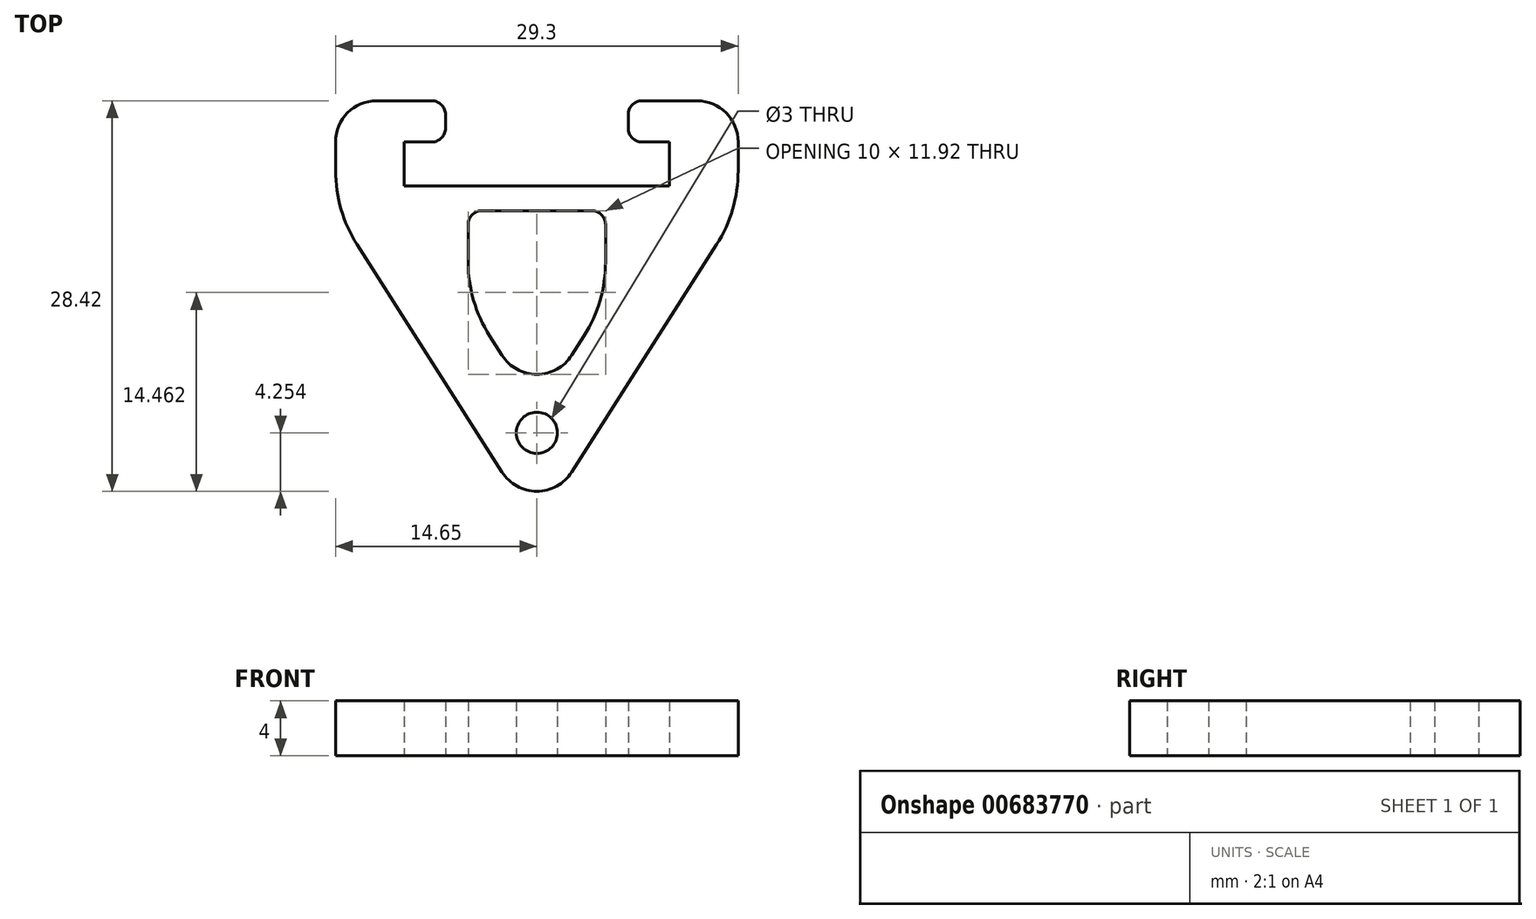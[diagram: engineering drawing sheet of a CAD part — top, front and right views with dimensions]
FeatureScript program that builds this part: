
annotation { "Feature Type Name" : "Feature", "Feature Type Description" : "" }
export const myFeature = defineFeature(function(context is Context, id is Id, definition is map)
    precondition{}
    {
        {
            assignVariable(context, id + "F0", {"name" : "thick", "anyValue" : 4});
        }
        {
            var Q0;
            Q0=qCreatedBy(makeId("Top.planeOp"),FACE);
            var sketch = newSketch(context, id + "F1", { "sketchPlane" : qUnion([Q0])});
            skLineSegment(sketch, "E0", {"start": v(-2.53, 3.97) * mm, "end": v(-13.08, 20.54) * mm});
            skLineSegment(sketch, "E1", {"start": v(13.08, 20.54) * mm, "end": v(2.53, 3.97) * mm});
            skLineSegment(sketch, "E2", {"start": v(0, 0) * mm, "end": v(0, 23) * mm, "construction": true});
            skLineSegment(sketch, "E3", {"start": v(5, 23) * mm, "end": v(-14.65, 23) * mm, "construction": true});
            skLineSegment(sketch, "E4", {"start": v(5, 23) * mm, "end": v(14.65, 23) * mm, "construction": true});
            skLineSegment(sketch, "E5", {"start": v(-14.65, 25.91) * mm, "end": v(-14.65, 28) * mm});
            skLineSegment(sketch, "E6", {"start": v(-11.65, 31) * mm, "end": v(-7.65, 31) * mm});
            skLineSegment(sketch, "E7", {"start": v(14.65, 28) * mm, "end": v(14.65, 25.91) * mm});
            skLineSegment(sketch, "E8", {"start": v(-7.65, 28) * mm, "end": v(-9.65, 28) * mm});
            skLineSegment(sketch, "E9", {"start": v(-9.65, 28) * mm, "end": v(-9.65, 24.8) * mm});
            skLineSegment(sketch, "E10", {"start": v(-9.65, 24.8) * mm, "end": v(9.65, 24.8) * mm});
            skLineSegment(sketch, "E11", {"start": v(-6.65, 29) * mm, "end": v(-6.65, 30) * mm});
            skLineSegment(sketch, "E12", {"start": v(-5, 22) * mm, "end": v(-5, 19.26) * mm});
            skLineSegment(sketch, "E13.MirrorCS", {"start": v(5, 22) * mm, "end": v(5, 19.26) * mm});
            skLineSegment(sketch, "E14.MirrorCS", {"start": v(9.65, 28) * mm, "end": v(9.65, 24.8) * mm});
            skLineSegment(sketch, "E15.MirrorCS", {"start": v(7.65, 28) * mm, "end": v(9.65, 28) * mm});
            skLineSegment(sketch, "E16.MirrorCS", {"start": v(6.65, 29) * mm, "end": v(6.65, 30) * mm});
            skLineSegment(sketch, "E17", {"start": v(-3.43, 13.9) * mm, "end": v(-2.53, 12.47) * mm});
            skLineSegment(sketch, "E18.MirrorCS", {"start": v(3.43, 13.9) * mm, "end": v(2.53, 12.47) * mm});
            skPoint(sketch, "E19.visualSharp", {"position": v(-14.65, 31) * mm});
            skArc(sketch, "E19.filletArc", {"start": v(-11.65, 31) * mm, "mid": v(-13.77, 30.12) * mm, "end": v(-14.65, 28) * mm});
            skPoint(sketch, "E20.visualSharp", {"position": v(14.65, 31) * mm});
            skArc(sketch, "E20.filletArc", {"start": v(14.65, 28) * mm, "mid": v(13.77, 30.12) * mm, "end": v(11.65, 31) * mm});
            skPoint(sketch, "E21.visualSharp", {"position": v(0, 8.5) * mm});
            skArc(sketch, "E21.filletArc", {"start": v(-2.53, 12.47) * mm, "mid": v(0, 11.08) * mm, "end": v(2.53, 12.47) * mm});
            skPoint(sketch, "E22.visualSharp", {"position": v(0, 0) * mm});
            skArc(sketch, "E22.filletArc", {"start": v(-2.53, 3.97) * mm, "mid": v(0, 2.58) * mm, "end": v(2.53, 3.97) * mm});
            skLineSegment(sketch, "E23.trimOffspring", {"start": v(7.65, 31) * mm, "end": v(11.65, 31) * mm});
            skPoint(sketch, "E24.visualSharp", {"position": v(-6.65, 31) * mm});
            skArc(sketch, "E24.filletArc", {"start": v(-6.65, 30) * mm, "mid": v(-6.94, 30.7) * mm, "end": v(-7.65, 31) * mm});
            skPoint(sketch, "E25.visualSharp", {"position": v(-6.65, 28) * mm});
            skArc(sketch, "E25.filletArc", {"start": v(-7.65, 28) * mm, "mid": v(-6.94, 28.3) * mm, "end": v(-6.65, 29) * mm});
            skPoint(sketch, "E26.visualSharp", {"position": v(6.65, 31) * mm});
            skArc(sketch, "E26.filletArc", {"start": v(7.65, 31) * mm, "mid": v(6.94, 30.7) * mm, "end": v(6.65, 30) * mm});
            skPoint(sketch, "E27.visualSharp", {"position": v(6.65, 28) * mm});
            skArc(sketch, "E27.filletArc", {"start": v(6.65, 29) * mm, "mid": v(6.94, 28.3) * mm, "end": v(7.65, 28) * mm});
            skPoint(sketch, "E28.visualSharp", {"position": v(-14.65, 23) * mm});
            skArc(sketch, "E28.filletArc", {"start": v(-14.65, 25.91) * mm, "mid": v(-14.25, 23.12) * mm, "end": v(-13.08, 20.54) * mm});
            skPoint(sketch, "E29.visualSharp", {"position": v(14.65, 23) * mm});
            skArc(sketch, "E29.filletArc", {"start": v(13.08, 20.54) * mm, "mid": v(14.25, 23.12) * mm, "end": v(14.65, 25.91) * mm});
            skPoint(sketch, "E30.visualSharp", {"position": v(-5, 16.35) * mm});
            skArc(sketch, "E30.filletArc", {"start": v(-5, 19.26) * mm, "mid": v(-4.6, 16.47) * mm, "end": v(-3.43, 13.9) * mm});
            skPoint(sketch, "E31.visualSharp", {"position": v(5, 16.35) * mm});
            skArc(sketch, "E31.filletArc", {"start": v(3.43, 13.9) * mm, "mid": v(4.6, 16.47) * mm, "end": v(5, 19.26) * mm});
            skCircle(sketch, "E32", {"center": v(0, 6.83) * mm, "radius": 1.5 * mm});
            skLineSegment(sketch, "E33", {"start": v(0, 11.08) * mm, "end": v(0, 2.58) * mm, "construction": true});
            skLineSegment(sketch, "E34", {"start": v(4, 23) * mm, "end": v(-4, 23) * mm});
            skPoint(sketch, "E35.newPointB", {"position": v(-5, 24.8) * mm});
            skArc(sketch, "E35.filletArc", {"start": v(-4, 23) * mm, "mid": v(-4.7, 22.7) * mm, "end": v(-5, 22) * mm});
            skPoint(sketch, "E36.newPointB", {"position": v(5, 24.8) * mm});
            skArc(sketch, "E36.filletArc", {"start": v(5, 22) * mm, "mid": v(4.7, 22.7) * mm, "end": v(4, 23) * mm});
            skSolve(sketch);
        }
        {
            var Q0;
            Q0=makeQuery(id+"F1.imprint","IMPRINT",FACE,{"disambiguationData":[TD([[makeQuery(id+"F1.imprint","IMPRINT",EDGE,{"derivedFrom":sQuery(id+"F1.wireOp",EDGE,"E0")}),-1.0]])]});
            var Q1;
            {var subQ5=sQuery(id+"F1.wireOp",EDGE,"E34");Q1=makeQuery(id+"F1.imprint","IMPRINT",FACE,{"disambiguationData":[TD([[makeQuery(id+"F1.imprint","IMPRINT",EDGE,{"derivedFrom":subQ5}),-1.0]])]});}
            extrude(context, id + "F2", {"entities" : qUnion([Q0, Q1]), "depth" : (getVariable(context, 'thick')) * mm, "offsetDistance" : 25 * mm});
        }
    });
